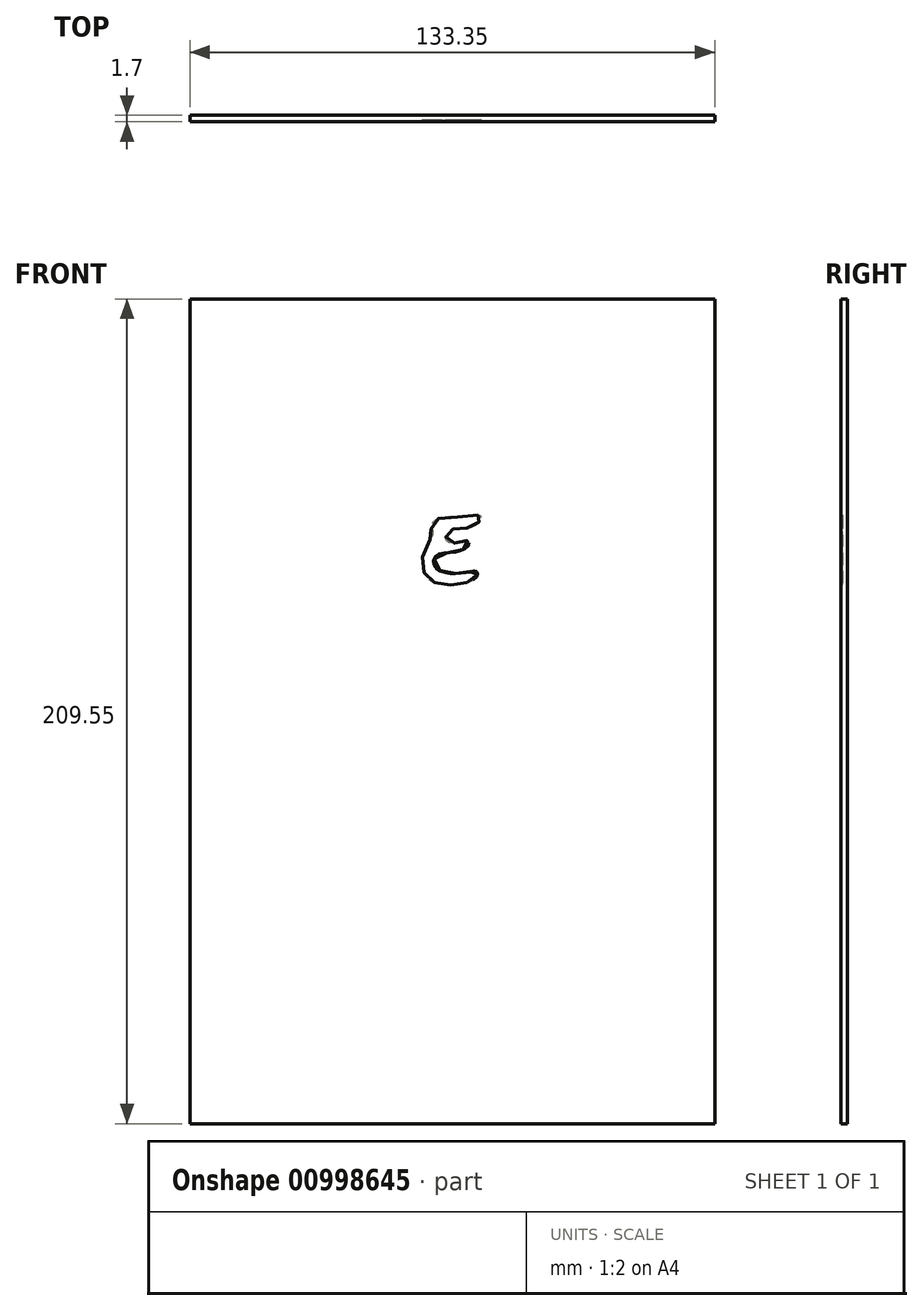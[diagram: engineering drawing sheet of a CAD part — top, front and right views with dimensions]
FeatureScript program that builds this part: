
annotation { "Feature Type Name" : "Feature", "Feature Type Description" : "" }
export const myFeature = defineFeature(function(context is Context, id is Id, definition is map)
    precondition{}
    {
        {
            var Q0;
            Q0=qCreatedBy(makeId("Front.planeOp"),FACE);
            var sketch = newSketch(context, id + "F0", { "sketchPlane" : qUnion([Q0])});
            skFitSpline(sketch, "E0", {"points": [v(-28.4, 65.87) * mm, v(-30.27, 65.68) * mm, v(-32.01, 65.5) * mm, v(-33.87, 65.36) * mm, v(-35.64, 65.42) * mm, v(-37.09, 65.36) * mm, v(-38.4, 65.07) * mm, v(-39.47, 64.43) * mm, v(-40.14, 63.65) * mm, v(-40.45, 62.98) * mm, v(-40.43, 62.58) * mm, v(-40.27, 62.3) * mm, v(-40.1, 62.15) * mm, v(-39.92, 61.97) * mm, v(-39.8, 61.68) * mm, v(-39.82, 61.25) * mm, v(-40.3, 60.22) * mm, v(-40.88, 59.1) * mm, v(-41.47, 57.81) * mm, v(-42.17, 56.3) * mm, v(-42.63, 54.65) * mm, v(-42.66, 53.5) * mm, v(-42.53, 52.56) * mm, v(-42.32, 51.7) * mm, v(-41.92, 50.86) * mm, v(-41.43, 50.14) * mm, v(-40.86, 49.53) * mm, v(-40.2, 49.02) * mm, v(-39.05, 48.55) * mm, v(-38.07, 48.34) * mm, v(-36.9, 48.19) * mm, v(-35.87, 48.16) * mm, v(-34.78, 48.15) * mm, v(-33.5, 48.24) * mm, v(-32.6, 48.38) * mm, v(-31.46, 48.63) * mm, v(-30.43, 49.01) * mm, v(-29.52, 49.51) * mm, v(-28.9, 50.07) * mm, v(-28.58, 50.55) * mm, v(-28.5, 50.92) * mm, v(-28.6, 51.3) * mm, v(-28.78, 51.5) * mm, v(-28.98, 51.64) * mm, v(-29.23, 51.7) * mm, v(-29.66, 51.65) * mm, v(-30.4, 51.48) * mm, v(-31.1, 51.35) * mm, v(-31.87, 51.25) * mm, v(-32.8, 51.16) * mm, v(-33.97, 51.08) * mm, v(-35, 51.08) * mm, v(-36.04, 51.14) * mm, v(-37.07, 51.36) * mm, v(-38.1, 51.75) * mm, v(-39, 52.3) * mm, v(-39.45, 52.92) * mm, v(-39.72, 53.57) * mm, v(-39.69, 54.43) * mm, v(-39.4, 55.13) * mm, v(-38.92, 55.73) * mm, v(-38.09, 56.02) * mm, v(-36.95, 56.2) * mm, v(-35.79, 56.3) * mm, v(-34.5, 56.47) * mm, v(-33.38, 56.73) * mm, v(-32.35, 57.04) * mm, v(-31.47, 57.48) * mm, v(-31.02, 57.9) * mm, v(-30.76, 58.5) * mm, v(-30.79, 58.99) * mm, v(-31.1, 59.4) * mm, v(-31.62, 59.54) * mm, v(-32.28, 59.38) * mm, v(-33.03, 59.1) * mm, v(-33.93, 58.84) * mm, v(-34.92, 58.7) * mm, v(-35.6, 58.84) * mm, v(-36.11, 59.11) * mm, v(-36.49, 59.53) * mm, v(-36.63, 60.04) * mm, v(-36.58, 60.58) * mm, v(-36.34, 61.14) * mm, v(-36.06, 61.54) * mm, v(-35.69, 61.9) * mm, v(-35.27, 62.18) * mm, v(-34.62, 62.37) * mm, v(-33.73, 62.47) * mm, v(-32.9, 62.48) * mm, v(-32.07, 62.5) * mm, v(-31.5, 62.53) * mm, v(-30.85, 62.62) * mm, v(-30.18, 62.82) * mm, v(-29.27, 63.23) * mm, v(-28.63, 63.68) * mm, v(-28.06, 64.17) * mm, v(-27.66, 64.64) * mm, v(-27.54, 65) * mm, v(-27.57, 65.3) * mm, v(-27.71, 65.57) * mm, v(-27.98, 65.78) * mm, v(-28.4, 65.87) * mm]});
            skLineSegment(sketch, "E1.bottom", {"start": v(-101.6, 120.8) * mm, "end": v(31.74, 120.8) * mm});
            skLineSegment(sketch, "E1.top", {"start": v(-101.6, -88.75) * mm, "end": v(31.74, -88.75) * mm});
            skLineSegment(sketch, "E1.left", {"start": v(-101.6, 120.8) * mm, "end": v(-101.6, -88.75) * mm});
            skLineSegment(sketch, "E1.right", {"start": v(31.74, 120.8) * mm, "end": v(31.74, -88.75) * mm});
            skLineSegment(sketch, "E2", {"start": v(-34.93, 120.8) * mm, "end": v(-34.93, -88.75) * mm, "construction": true});
            skLineSegment(sketch, "E3", {"start": v(-101.6, 57.3) * mm, "end": v(31.74, 57.3) * mm, "construction": true});
            skLineSegment(sketch, "E4", {"start": v(-42.87, 57.3) * mm, "end": v(-44.63, 57.3) * mm, "construction": true});
            skLineSegment(sketch, "E5", {"start": v(-34.93, 66.83) * mm, "end": v(-34.93, 71.8) * mm, "construction": true});
            skLineSegment(sketch, "E6", {"start": v(-34.93, 71.8) * mm, "end": v(-35.1, 71.8) * mm, "construction": true});
            skPoint(sketch, "E7.orphan", {"position": v(-42.87, 66.83) * mm});
            skPoint(sketch, "E8.orphan", {"position": v(-42.87, 47.78) * mm});
            skPoint(sketch, "E9.right.start.orphan", {"position": v(-27, 66.83) * mm});
            skFitSpline(sketch, "E10.0", {"points": [v(-28.12, 65.9) * mm, v(-28.38, 65.93) * mm, v(-28.78, 65.9) * mm, v(-29.28, 65.85) * mm, v(-29.82, 65.79) * mm, v(-30.53, 65.7) * mm, v(-31.14, 65.64) * mm, v(-31.74, 65.58) * mm, v(-32.35, 65.52) * mm, v(-33, 65.45) * mm, v(-33.64, 65.41) * mm, v(-34.29, 65.4) * mm, v(-35.08, 65.45) * mm, v(-35.99, 65.49) * mm, v(-36.83, 65.45) * mm, v(-37.66, 65.35) * mm, v(-38.46, 65.13) * mm, v(-39.07, 64.81) * mm, v(-39.49, 64.5) * mm, v(-39.85, 64.14) * mm, v(-40.14, 63.76) * mm, v(-40.36, 63.37) * mm, v(-40.48, 63.09) * mm, v(-40.53, 62.83) * mm, v(-40.5, 62.6) * mm, v(-40.4, 62.4) * mm, v(-40.28, 62.22) * mm, v(-40.14, 62.12) * mm, v(-40.02, 62.02) * mm, v(-39.91, 61.88) * mm, v(-39.84, 61.7) * mm, v(-39.82, 61.5) * mm, v(-39.86, 61.27) * mm, v(-39.98, 60.96) * mm, v(-40.15, 60.6) * mm, v(-40.34, 60.23) * mm, v(-40.53, 59.88) * mm, v(-40.72, 59.54) * mm, v(-40.96, 59.07) * mm, v(-41.19, 58.57) * mm, v(-41.42, 58.04) * mm, v(-41.67, 57.52) * mm, v(-41.94, 56.98) * mm, v(-42.19, 56.4) * mm, v(-42.42, 55.8) * mm, v(-42.6, 55.18) * mm, v(-42.7, 54.6) * mm, v(-42.75, 54.07) * mm, v(-42.72, 53.46) * mm, v(-42.64, 52.89) * mm, v(-42.56, 52.44) * mm, v(-42.5, 52.11) * mm, v(-42.41, 51.79) * mm, v(-42.25, 51.36) * mm, v(-41.98, 50.84) * mm, v(-41.68, 50.37) * mm, v(-41.4, 50.03) * mm, v(-41.18, 49.78) * mm, v(-40.96, 49.55) * mm, v(-40.73, 49.34) * mm, v(-40.48, 49.14) * mm, v(-40.19, 48.95) * mm, v(-39.83, 48.78) * mm, v(-39.45, 48.62) * mm, v(-39.06, 48.5) * mm, v(-38.71, 48.4) * mm, v(-38.38, 48.34) * mm, v(-37.9, 48.26) * mm, v(-37.38, 48.18) * mm, v(-36.87, 48.13) * mm, v(-36.38, 48.11) * mm, v(-35.91, 48.11) * mm, v(-35.44, 48.1) * mm, v(-35.07, 48.1) * mm, v(-34.68, 48.1) * mm, v(-34.12, 48.12) * mm, v(-33.57, 48.17) * mm, v(-33.12, 48.24) * mm, v(-32.8, 48.3) * mm, v(-32.47, 48.35) * mm, v(-32.1, 48.42) * mm, v(-31.7, 48.5) * mm, v(-31.2, 48.64) * mm, v(-30.74, 48.82) * mm, v(-30.3, 49.02) * mm, v(-29.96, 49.18) * mm, v(-29.64, 49.36) * mm, v(-29.26, 49.63) * mm, v(-28.87, 50.01) * mm, v(-28.53, 50.47) * mm, v(-28.43, 50.84) * mm, v(-28.5, 51.16) * mm, v(-28.58, 51.37) * mm, v(-28.71, 51.52) * mm, v(-28.86, 51.63) * mm, v(-29.02, 51.71) * mm, v(-29.2, 51.76) * mm, v(-29.43, 51.75) * mm, v(-29.69, 51.7) * mm, v(-29.99, 51.63) * mm, v(-30.3, 51.55) * mm, v(-30.6, 51.49) * mm, v(-30.9, 51.43) * mm, v(-31.18, 51.39) * mm, v(-31.58, 51.33) * mm, v(-32.1, 51.27) * mm, v(-32.8, 51.21) * mm, v(-33.44, 51.16) * mm, v(-33.95, 51.13) * mm, v(-34.44, 51.12) * mm, v(-35.03, 51.13) * mm, v(-35.75, 51.15) * mm, v(-36.46, 51.25) * mm, v(-37.04, 51.4) * mm, v(-37.5, 51.56) * mm, v(-37.84, 51.7) * mm, v(-38.19, 51.84) * mm, v(-38.52, 52.02) * mm, v(-38.83, 52.22) * mm, v(-39.06, 52.43) * mm, v(-39.24, 52.68) * mm, v(-39.4, 52.93) * mm, v(-39.54, 53.19) * mm, v(-39.65, 53.45) * mm, v(-39.7, 53.75) * mm, v(-39.7, 54.08) * mm, v(-39.65, 54.41) * mm, v(-39.55, 54.7) * mm, v(-39.43, 54.97) * mm, v(-39.28, 55.24) * mm, v(-39.1, 55.5) * mm, v(-38.9, 55.7) * mm, v(-38.62, 55.83) * mm, v(-38.3, 55.93) * mm, v(-37.95, 56) * mm, v(-37.45, 56.08) * mm, v(-36.81, 56.16) * mm, v(-36.2, 56.2) * mm, v(-35.67, 56.25) * mm, v(-35.13, 56.31) * mm, v(-34.45, 56.41) * mm, v(-33.83, 56.56) * mm, v(-33.36, 56.69) * mm, v(-32.88, 56.8) * mm, v(-32.4, 56.95) * mm, v(-31.95, 57.15) * mm, v(-31.63, 57.32) * mm, v(-31.36, 57.49) * mm, v(-31.14, 57.66) * mm, v(-30.96, 57.88) * mm, v(-30.81, 58.14) * mm, v(-30.72, 58.43) * mm, v(-30.68, 58.7) * mm, v(-30.7, 58.96) * mm, v(-30.83, 59.2) * mm, v(-31.02, 59.41) * mm, v(-31.26, 59.55) * mm, v(-31.54, 59.6) * mm, v(-31.82, 59.57) * mm, v(-32.11, 59.5) * mm, v(-32.5, 59.36) * mm, v(-32.9, 59.2) * mm, v(-33.3, 59.06) * mm, v(-33.64, 58.97) * mm, v(-33.98, 58.88) * mm, v(-34.34, 58.8) * mm, v(-34.69, 58.76) * mm, v(-35.01, 58.75) * mm, v(-35.3, 58.8) * mm, v(-35.57, 58.88) * mm, v(-35.82, 58.98) * mm, v(-36.04, 59.12) * mm, v(-36.24, 59.28) * mm, v(-36.4, 59.48) * mm, v(-36.52, 59.7) * mm, v(-36.57, 59.95) * mm, v(-36.59, 60.2) * mm, v(-36.56, 60.45) * mm, v(-36.5, 60.7) * mm, v(-36.38, 60.96) * mm, v(-36.25, 61.2) * mm, v(-36.12, 61.39) * mm, v(-35.97, 61.57) * mm, v(-35.79, 61.75) * mm, v(-35.6, 61.91) * mm, v(-35.4, 62.05) * mm, v(-35.18, 62.17) * mm, v(-34.92, 62.25) * mm, v(-34.62, 62.32) * mm, v(-34.3, 62.37) * mm, v(-33.96, 62.4) * mm, v(-33.52, 62.43) * mm, v(-33.1, 62.43) * mm, v(-32.65, 62.44) * mm, v(-32.32, 62.45) * mm, v(-32.02, 62.46) * mm, v(-31.76, 62.47) * mm, v(-31.5, 62.48) * mm, v(-31.21, 62.5) * mm, v(-30.92, 62.55) * mm, v(-30.64, 62.62) * mm, v(-30.36, 62.7) * mm, v(-29.95, 62.85) * mm, v(-29.48, 63.05) * mm, v(-29.08, 63.28) * mm, v(-28.83, 63.46) * mm, v(-28.6, 63.65) * mm, v(-28.27, 63.9) * mm, v(-27.96, 64.18) * mm, v(-27.7, 64.47) * mm, v(-27.56, 64.7) * mm, v(-27.5, 64.92) * mm, v(-27.48, 65.2) * mm, v(-27.56, 65.46) * mm, v(-27.75, 65.69) * mm, v(-27.93, 65.82) * mm, v(-28.12, 65.9) * mm, v(-28.38, 65.93) * mm, v(-28.78, 65.9) * mm, v(-28.12, 65.9) * mm]});
            skSolve(sketch);
        }
        {
            var Q0;
            Q0=makeQuery(id+"F0.imprint","IMPRINT",FACE,{"disambiguationData":[TD([[makeQuery(id+"F0.imprint","IMPRINT",EDGE,{"derivedFrom":sQuery(id+"F0.wireOp",EDGE,"E1.bottom")}),-1.0]])]});
            extrude(context, id + "F1", {"entities" : qUnion([Q0]), "depth" : 1.7 * mm, "offsetDistance" : 25.4 * mm});
        }
        {
            var Q0;
            Q0=makeQuery(id+"F0.imprint","IMPRINT",FACE,{"disambiguationData":[TD([[makeQuery(id+"F0.imprint","IMPRINT",EDGE,{"derivedFrom":sQuery(id+"F0.wireOp",EDGE,"E0")}),1.0]])]});
            var Q1;
            Q1=makeQuery(id+"F0.imprint","IMPRINT",FACE,{"disambiguationData":[TD([[makeQuery(id+"F0.imprint","IMPRINT",EDGE,{"derivedFrom":sQuery(id+"F0.wireOp",EDGE,"E0")}),-1.0]])]});
            extrude(context, id + "F2", {"entities" : qUnion([Q0, Q1]), "operationType" : NewBodyOperationType.ADD, "depth" : 1.27 * mm, "offsetDistance" : 25.4 * mm});
        }
    });
